# Revit family: Haworth_BuzziBalance_SmallPouf
name_source: partatom
category: Furniture
revit_build: Autodesk Revit 2018 (Build: 20170223_1515(x64)
units: mm (PartAtom-declared; Revit-internal decimal feet)

## family parameters
Always vertical = Yes
Cut with Voids When Loaded = No
OmniClass Number = 23.40.70.14.64.21
OmniClass Title = Systems Furniture
Room Calculation Point = No
Shared = No
Work Plane-Based = No

## types (2) — shared parameters
Actual Depth = 22.05 "
Actual Width = 22.05 "
Assembly Code = E2020200
Base Finish = Haworth _ Wood _ Collection _ Ash Natural
Manufacturer = Haworth
Model = HCBZ-BAP
Radius = 11.03 "
Revision Number = 1
Size = Verify Final Dim. w/ Haworth
URL = http://www.haworth.com
URL - Product = https://www.haworth.com
Warranty = http://www.haworth.com

## per-type parameters (varying)
| type | Actual Height | Description | High | Low |
| HCBZ-BAP1-2 - Low | 14.96 " | Haworth BuzziBalance Low Small Pouf | No | Yes |
| HCBZ-BAP2-2 - High | 18.31 " | Haworth BuzziBalance High Small Pouf | Yes | No |

## geometry (parser evidence)
native form markers: Sweep x3
no freeform markers — native parametric forms only
